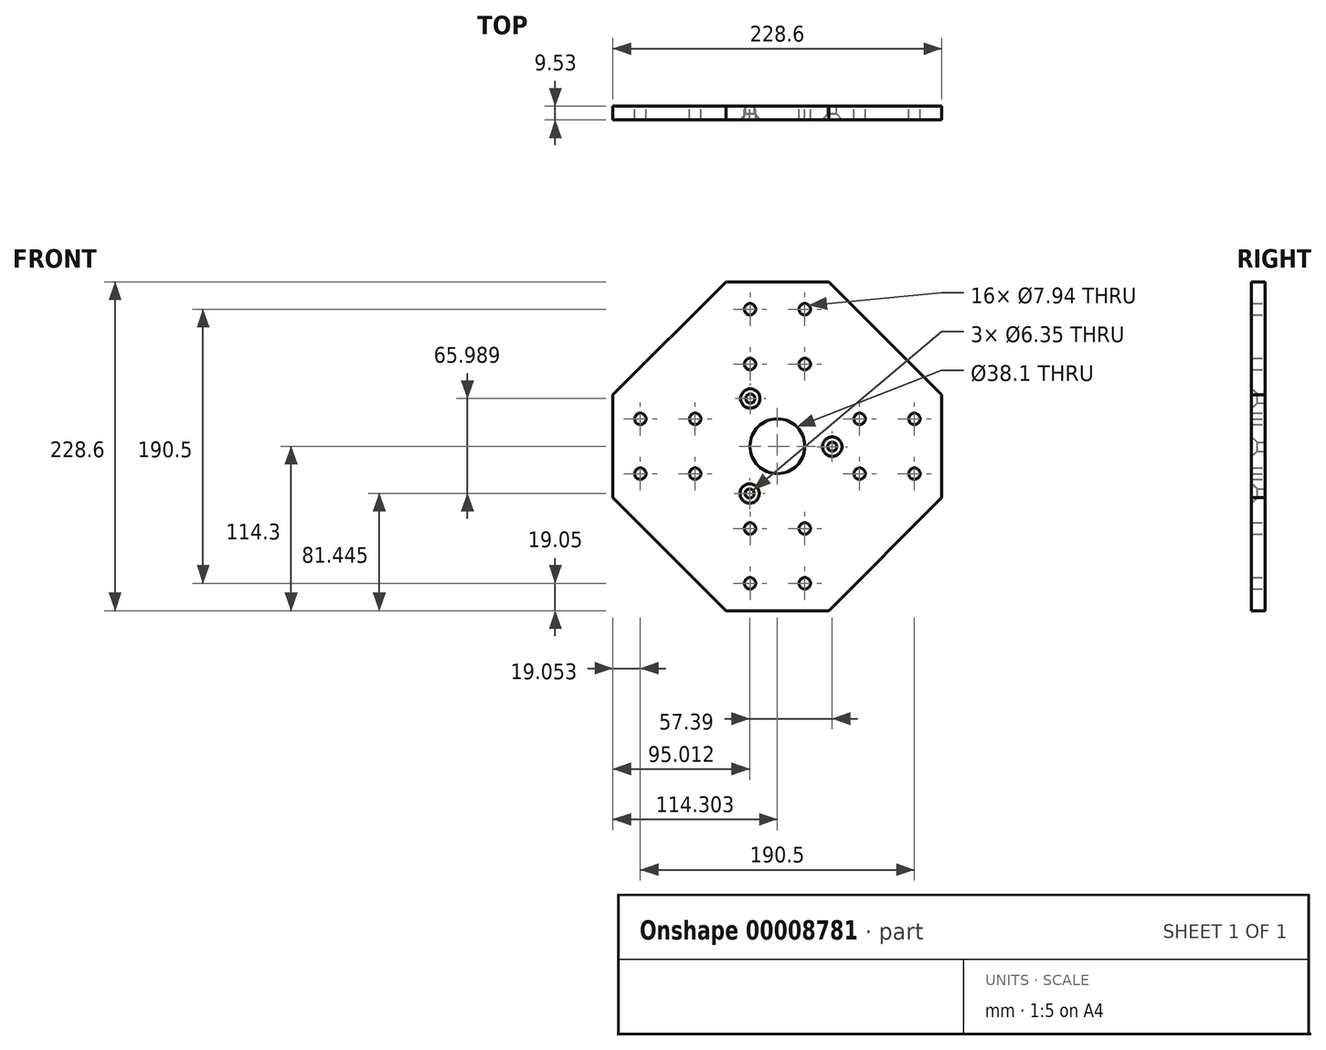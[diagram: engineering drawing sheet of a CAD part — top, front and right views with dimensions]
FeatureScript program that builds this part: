
annotation { "Feature Type Name" : "Feature", "Feature Type Description" : "" }
export const myFeature = defineFeature(function(context is Context, id is Id, definition is map)
    precondition{}
    {
        {
            var Q0;
            Q0=qCreatedBy(makeId("Front.planeOp"),FACE);
            var sketch = newSketch(context, id + "F0", { "sketchPlane" : qUnion([Q0])});
            skCircle(sketch, "E0", {"center": v(-193.23, 0) * mm, "radius": 44.45 * mm, "construction": true});
            skCircle(sketch, "E1", {"center": v(-193.23, 0) * mm, "radius": 19.05 * mm});
            skCircle(sketch, "E2", {"center": v(-212.04, 33.13) * mm, "radius": 3.18 * mm});
            skCircle(sketch, "E3.1.0", {"center": v(-155.13, -0.28) * mm, "radius": 3.17 * mm});
            skCircle(sketch, "E3.2.0", {"center": v(-212.52, -32.86) * mm, "radius": 3.18 * mm});
            skLineSegment(sketch, "E3.anchor1", {"start": v(-193.23, 0) * mm, "end": v(-212.04, 33.13) * mm, "construction": true});
            skLineSegment(sketch, "E3.anchor2", {"start": v(-193.23, 0) * mm, "end": v(-212.52, -32.86) * mm, "construction": true});
            skLineSegment(sketch, "E4.bottom", {"start": v(-155.13, 38.1) * mm, "end": v(-231.33, 38.1) * mm, "construction": true});
            skLineSegment(sketch, "E4.top", {"start": v(-155.13, -38.1) * mm, "end": v(-231.33, -38.1) * mm, "construction": true});
            skLineSegment(sketch, "E4.left", {"start": v(-155.13, 38.1) * mm, "end": v(-155.13, -38.1) * mm, "construction": true});
            skLineSegment(sketch, "E4.right", {"start": v(-231.33, 38.1) * mm, "end": v(-231.33, -38.1) * mm, "construction": true});
            skLineSegment(sketch, "E5.anchor2", {"start": v(-193.23, 0) * mm, "end": v(-149.04, 4.79) * mm, "construction": true});
            skLineSegment(sketch, "E6", {"start": v(-228.91, 114.3) * mm, "end": v(-157.54, 114.3) * mm});
            skLineSegment(sketch, "E7", {"start": v(-78.93, 35.69) * mm, "end": v(-78.93, -35.69) * mm});
            skLineSegment(sketch, "E8", {"start": v(-307.53, -35.69) * mm, "end": v(-307.53, 35.69) * mm});
            skLineSegment(sketch, "E9", {"start": v(-228.91, -114.3) * mm, "end": v(-157.54, -114.3) * mm});
            skLineSegment(sketch, "E10", {"start": v(-228.91, -38.1) * mm, "end": v(-228.91, -114.3) * mm, "construction": true});
            skLineSegment(sketch, "E11", {"start": v(-228.91, -114.3) * mm, "end": v(-157.54, -114.3) * mm, "construction": true});
            skLineSegment(sketch, "E12", {"start": v(-157.54, -114.3) * mm, "end": v(-157.54, -38.1) * mm, "construction": true});
            skLineSegment(sketch, "E13", {"start": v(-157.54, -38.1) * mm, "end": v(-228.91, -38.1) * mm, "construction": true});
            skCircle(sketch, "E14", {"center": v(-212.26, -57.15) * mm, "radius": 3.97 * mm});
            skCircle(sketch, "E15", {"center": v(-174.19, -57.15) * mm, "radius": 3.97 * mm});
            skCircle(sketch, "E16", {"center": v(-212.26, -95.25) * mm, "radius": 3.97 * mm});
            skCircle(sketch, "E17", {"center": v(-174.19, -95.25) * mm, "radius": 3.97 * mm});
            skLineSegment(sketch, "E18.1.0", {"start": v(-228.91, 38.1) * mm, "end": v(-157.54, 38.1) * mm, "construction": true});
            skCircle(sketch, "E19.1.0", {"center": v(-136.08, 19.04) * mm, "radius": 3.97 * mm});
            skLineSegment(sketch, "E19.1.1", {"start": v(-78.93, 35.69) * mm, "end": v(-155.13, 35.69) * mm, "construction": true});
            skCircle(sketch, "E19.1.2", {"center": v(-136.08, -19.04) * mm, "radius": 3.97 * mm});
            skCircle(sketch, "E19.1.3", {"center": v(-97.98, -19.04) * mm, "radius": 3.97 * mm});
            skCircle(sketch, "E19.1.4", {"center": v(-97.98, 19.04) * mm, "radius": 3.97 * mm});
            skLineSegment(sketch, "E19.1.5", {"start": v(-155.13, -35.69) * mm, "end": v(-78.93, -35.69) * mm, "construction": true});
            skLineSegment(sketch, "E19.1.6", {"start": v(-155.13, 35.69) * mm, "end": v(-155.13, -35.69) * mm, "construction": true});
            skCircle(sketch, "E19.2.0", {"center": v(-212.26, 57.15) * mm, "radius": 3.97 * mm});
            skLineSegment(sketch, "E19.2.1", {"start": v(-228.91, 114.3) * mm, "end": v(-228.91, 38.1) * mm, "construction": true});
            skCircle(sketch, "E19.2.2", {"center": v(-174.19, 57.15) * mm, "radius": 3.97 * mm});
            skCircle(sketch, "E19.2.3", {"center": v(-174.19, 95.25) * mm, "radius": 3.97 * mm});
            skCircle(sketch, "E19.2.4", {"center": v(-212.26, 95.25) * mm, "radius": 3.97 * mm});
            skLineSegment(sketch, "E19.2.5", {"start": v(-157.54, 38.1) * mm, "end": v(-157.54, 114.3) * mm, "construction": true});
            skCircle(sketch, "E19.3.0", {"center": v(-250.38, -19.04) * mm, "radius": 3.97 * mm});
            skLineSegment(sketch, "E19.3.1", {"start": v(-307.53, -35.69) * mm, "end": v(-231.33, -35.69) * mm, "construction": true});
            skCircle(sketch, "E19.3.2", {"center": v(-250.38, 19.04) * mm, "radius": 3.97 * mm});
            skCircle(sketch, "E19.3.3", {"center": v(-288.48, 19.04) * mm, "radius": 3.97 * mm});
            skCircle(sketch, "E19.3.4", {"center": v(-288.48, -19.04) * mm, "radius": 3.97 * mm});
            skLineSegment(sketch, "E19.3.5", {"start": v(-231.33, 35.69) * mm, "end": v(-307.53, 35.69) * mm, "construction": true});
            skLineSegment(sketch, "E19.3.6", {"start": v(-231.33, -35.69) * mm, "end": v(-231.33, 35.69) * mm, "construction": true});
            skLineSegment(sketch, "E20", {"start": v(-307.53, 35.69) * mm, "end": v(-228.91, 114.3) * mm});
            skLineSegment(sketch, "E21", {"start": v(-157.54, 114.3) * mm, "end": v(-78.93, 35.69) * mm});
            skLineSegment(sketch, "E22", {"start": v(-78.93, -35.69) * mm, "end": v(-157.54, -114.3) * mm});
            skLineSegment(sketch, "E23", {"start": v(-228.91, -114.3) * mm, "end": v(-307.53, -35.69) * mm});
            skSolve(sketch);
        }
        {
            var Q0;
            Q0=makeQuery(id+"F0.imprint","IMPRINT",FACE,{"disambiguationData":[TD([[makeQuery(id+"F0.imprint","IMPRINT",EDGE,{"derivedFrom":sQuery(id+"F0.wireOp",EDGE,"E1")}),-1.0]])]});
            extrude(context, id + "F1", {"entities" : qUnion([Q0]), "depth" : 9.52 * mm});
        }
        {
            var Q0;
            Q0=makeQuery(id+"F1.opExtrude","CAP_EDGE",EDGE,{"disambiguationData":[OSD([sQuery(id+"F0.wireOp",EDGE,"E3.1.0")])],"isStart":false});
            var Q1;
            Q1=makeQuery(id+"F1.opExtrude","CAP_EDGE",EDGE,{"disambiguationData":[OSD([sQuery(id+"F0.wireOp",EDGE,"E2")])],"isStart":false});
            var Q2;
            Q2=makeQuery(id+"F1.opExtrude","CAP_EDGE",EDGE,{"disambiguationData":[OSD([sQuery(id+"F0.wireOp",EDGE,"E3.2.0")])],"isStart":false});
            chamfer(context, id + "F2", {"entities" : qUnion([Q0, Q1, Q2]), "chamferType" : ChamferType.OFFSET_ANGLE, "width" : 4.1 * mm, "oppositeDirection" : false, "angle" : 41 * degree, "tangentPropagation" : true});
        }
    });
